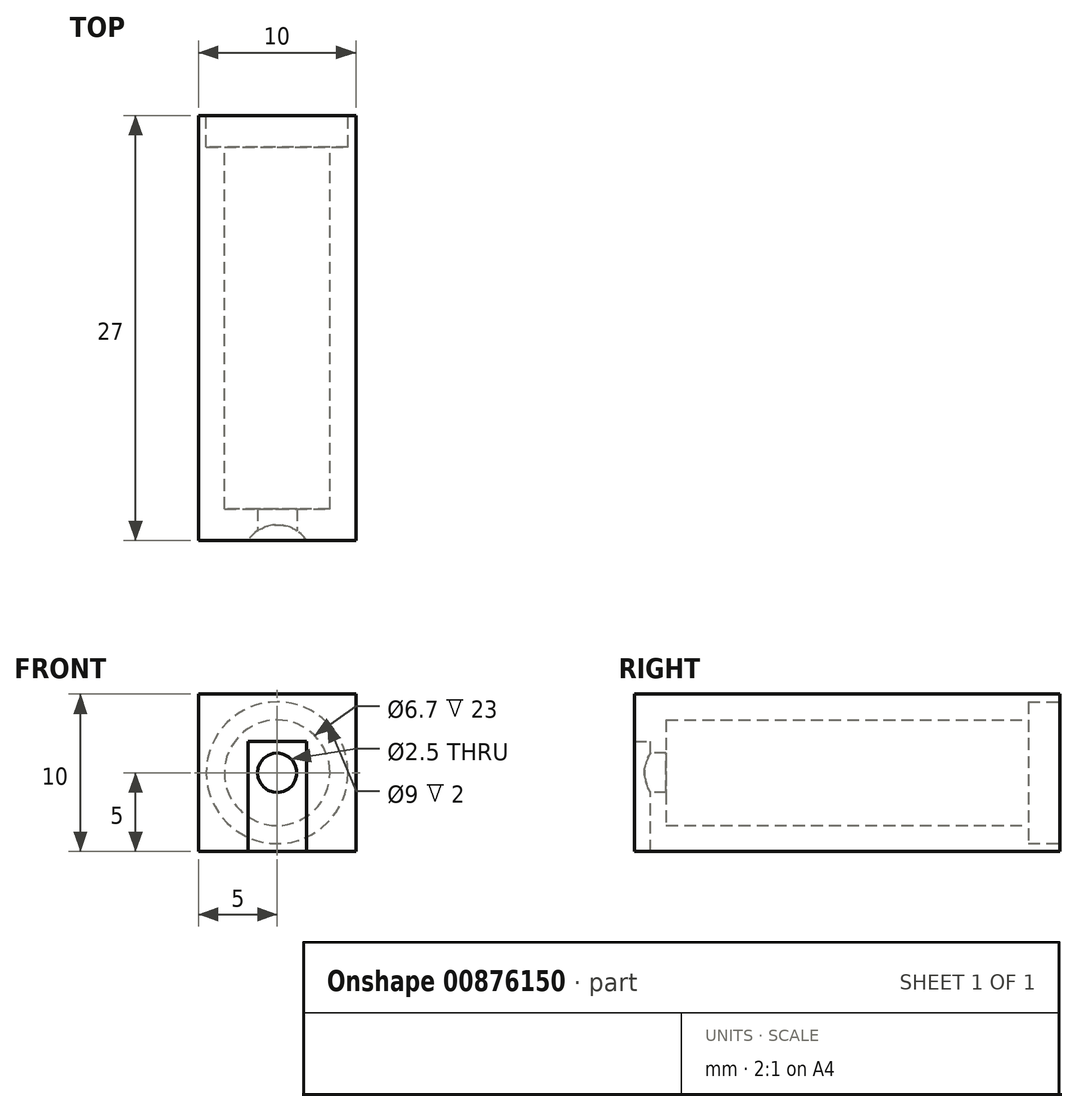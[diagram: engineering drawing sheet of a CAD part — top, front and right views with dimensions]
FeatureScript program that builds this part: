
annotation { "Feature Type Name" : "Feature", "Feature Type Description" : "" }
export const myFeature = defineFeature(function(context is Context, id is Id, definition is map)
    precondition{}
    {
        {
            var Q0;
            Q0=qCreatedBy(makeId("Front.planeOp"),FACE);
            var sketch = newSketch(context, id + "F0", { "sketchPlane" : qUnion([Q0])});
            skLineSegment(sketch, "E0.bottom", {"start": v(5, -5) * mm, "end": v(-5, -5) * mm});
            skLineSegment(sketch, "E0.top", {"start": v(5, 5) * mm, "end": v(-5, 5) * mm});
            skLineSegment(sketch, "E0.left", {"start": v(5, -5) * mm, "end": v(5, 5) * mm});
            skLineSegment(sketch, "E0.right", {"start": v(-5, -5) * mm, "end": v(-5, 5) * mm});
            skPoint(sketch, "E0.middle", {"position": v(0, 0) * mm});
            skSolve(sketch);
        }
        {
            var Q0;
            Q0 = qSketchRegion(id + "F0", true);
            extrude(context, id + "F1", {"entities" : qUnion([Q0]), "oppositeDirection" : true, "depth" : 27 * mm, "offsetDistance" : 25 * mm});
        }
        {
            var Q0;
            Q0=makeQuery(id+"F1.opExtrude","CAP_FACE",FACE,{"disambiguationData":[OSD([sQuery(id+"F0.wireOp",EDGE,"E0.bottom"),sQuery(id+"F0.wireOp",EDGE,"E0.top"),sQuery(id+"F0.wireOp",EDGE,"E0.left"),sQuery(id+"F0.wireOp",EDGE,"E0.right")])],"isStart":true});
            var sketch = newSketch(context, id + "F2", { "sketchPlane" : qUnion([Q0])});
            skCircle(sketch, "E1", {"center": v(0, 0) * mm, "radius": 1.25 * mm});
            skSolve(sketch);
        }
        {
            var Q0;
            Q0 = qSketchRegion(id + "F2", true);
            extrude(context, id + "F3", {"entities" : qUnion([Q0]), "operationType" : NewBodyOperationType.REMOVE, "oppositeDirection" : true, "depth" : 25 * mm, "offsetDistance" : 25 * mm});
        }
        {
            var Q0;
            Q0=qCreatedBy(makeId("Top.planeOp"),FACE);
            var sketch = newSketch(context, id + "F4", { "sketchPlane" : qUnion([Q0])});
            skCircle(sketch, "E2", {"center": v(0, -1.23) * mm, "radius": 2.23 * mm});
            skSolve(sketch);
        }
        {
            var Q0;
            Q0 = qSketchRegion(id + "F4", true);
            extrude(context, id + "F5", {"entities" : qUnion([Q0]), "operationType" : NewBodyOperationType.REMOVE, "oppositeDirection" : true, "depth" : 25 * mm, "offsetDistance" : 25 * mm});
        }
        {
            var Q0;
            Q0 = qSketchRegion(id + "F4", true);
            extrude(context, id + "F6", {"entities" : qUnion([Q0]), "operationType" : NewBodyOperationType.REMOVE, "depth" : 2 * mm, "offsetDistance" : 25 * mm});
        }
        {
            var Q0;
            Q0=makeQuery(id+"F1.opExtrude","CAP_FACE",FACE,{"disambiguationData":[OSD([sQuery(id+"F0.wireOp",EDGE,"E0.bottom"),sQuery(id+"F0.wireOp",EDGE,"E0.top"),sQuery(id+"F0.wireOp",EDGE,"E0.left"),sQuery(id+"F0.wireOp",EDGE,"E0.right")])],"isStart":false});
            var sketch = newSketch(context, id + "F7", { "sketchPlane" : qUnion([Q0])});
            skCircle(sketch, "E3", {"center": v(0, 0) * mm, "radius": 3.35 * mm});
            skSolve(sketch);
        }
        {
            var Q0;
            Q0 = qSketchRegion(id + "F7", true);
            extrude(context, id + "F8", {"entities" : qUnion([Q0]), "operationType" : NewBodyOperationType.REMOVE, "oppositeDirection" : true, "depth" : 25 * mm, "offsetDistance" : 25 * mm});
        }
        {
            var Q0;
            Q0=makeQuery(id+"F1.opExtrude","CAP_FACE",FACE,{"disambiguationData":[OSD([sQuery(id+"F0.wireOp",EDGE,"E0.bottom"),sQuery(id+"F0.wireOp",EDGE,"E0.top"),sQuery(id+"F0.wireOp",EDGE,"E0.left"),sQuery(id+"F0.wireOp",EDGE,"E0.right")])],"isStart":false});
            var sketch = newSketch(context, id + "F9", { "sketchPlane" : qUnion([Q0])});
            skCircle(sketch, "E4", {"center": v(0, 0) * mm, "radius": 4.5 * mm});
            skSolve(sketch);
        }
        {
            var Q0;
            Q0 = qSketchRegion(id + "F9", true);
            extrude(context, id + "F10", {"entities" : qUnion([Q0]), "operationType" : NewBodyOperationType.REMOVE, "oppositeDirection" : true, "depth" : 2 * mm, "offsetDistance" : 25 * mm});
        }
    });
